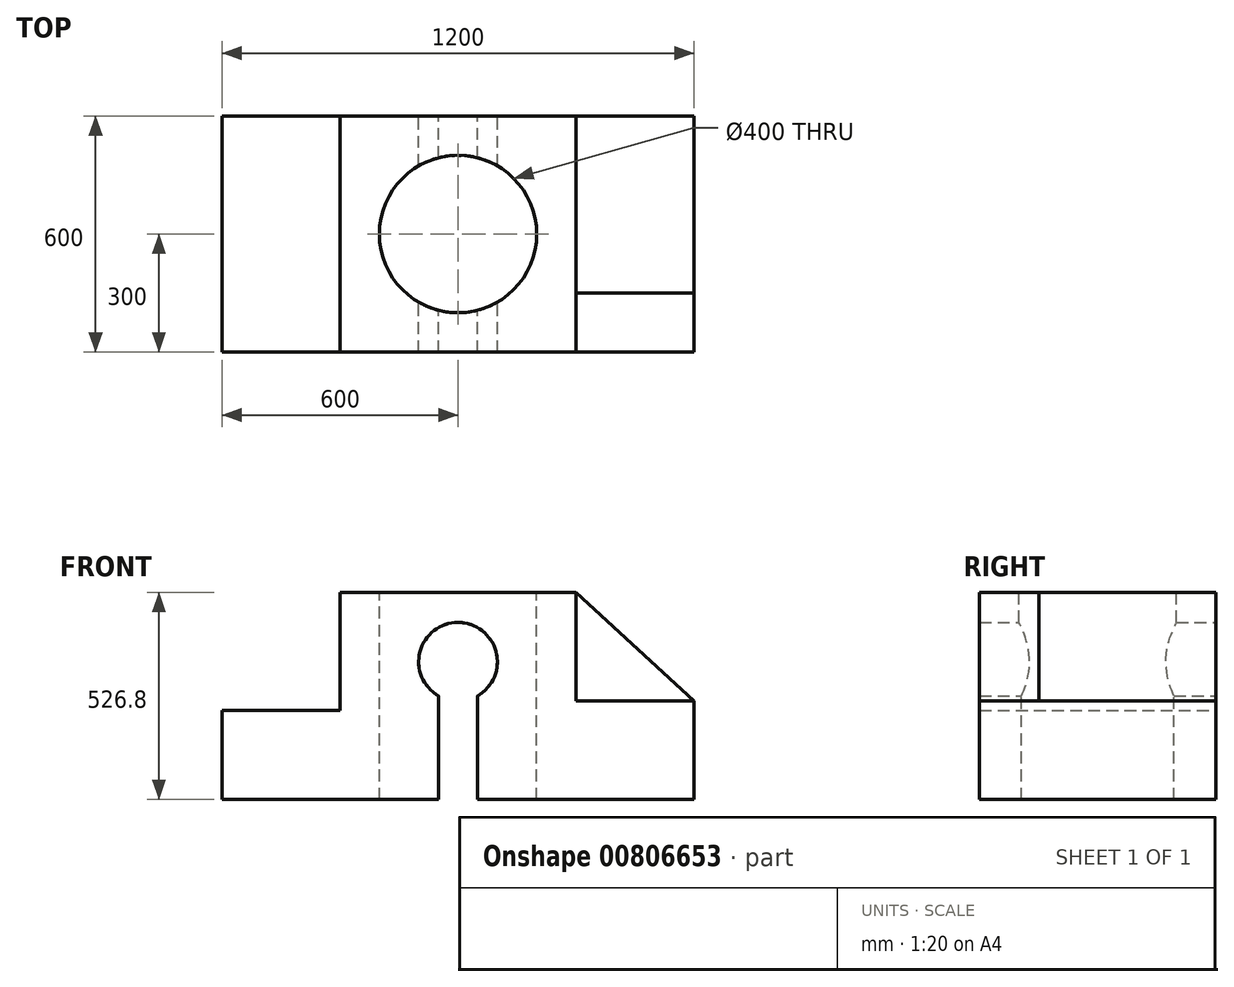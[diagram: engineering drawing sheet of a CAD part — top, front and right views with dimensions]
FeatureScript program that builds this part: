
annotation { "Feature Type Name" : "Feature", "Feature Type Description" : "" }
export const myFeature = defineFeature(function(context is Context, id is Id, definition is map)
    precondition{}
    {
        {
            var Q0;
            Q0=qCreatedBy(makeId("Front.planeOp"),FACE);
            var sketch = newSketch(context, id + "F0", { "sketchPlane" : qUnion([Q0])});
            skLineSegment(sketch, "E0.bottom", {"start": v(300, 263.4) * mm, "end": v(-300, 263.4) * mm});
            skLineSegment(sketch, "E0.top", {"start": v(600, -263.4) * mm, "end": v(50, -263.4) * mm});
            skLineSegment(sketch, "E0.left", {"start": v(600, -13.4) * mm, "end": v(600, -263.4) * mm});
            skLineSegment(sketch, "E0.right", {"start": v(-600, -36.6) * mm, "end": v(-600, -263.4) * mm});
            skPoint(sketch, "E0.middle", {"position": v(0, 0) * mm});
            skLineSegment(sketch, "E1", {"start": v(300, 263.4) * mm, "end": v(300, -13.4) * mm});
            skLineSegment(sketch, "E2", {"start": v(300, -13.4) * mm, "end": v(600, -13.4) * mm});
            skLineSegment(sketch, "E3", {"start": v(-300, 263.4) * mm, "end": v(-300, -36.6) * mm});
            skLineSegment(sketch, "E4", {"start": v(-300, -36.6) * mm, "end": v(-600, -36.6) * mm});
            skLineSegment(sketch, "E5", {"start": v(600, -263.4) * mm, "end": v(600, -13.4) * mm});
            skPoint(sketch, "E6.orphan", {"position": v(-600, 263.4) * mm});
            skPoint(sketch, "E7.orphan", {"position": v(600, 263.4) * mm});
            skArc(sketch, "E8", {"start": v(50, 0) * mm, "mid": v(0, 186.6) * mm, "end": v(-50, 0) * mm});
            skLineSegment(sketch, "E9.left", {"start": v(50, 0) * mm, "end": v(50, -263.4) * mm});
            skLineSegment(sketch, "E9.right", {"start": v(-50, 0) * mm, "end": v(-50, -263.4) * mm});
            skPoint(sketch, "E9.middle", {"position": v(0, -263.4) * mm});
            skPoint(sketch, "E10.orphan", {"position": v(-50, -526.8) * mm});
            skPoint(sketch, "E11.orphan", {"position": v(50, -526.8) * mm});
            skLineSegment(sketch, "E12.trimOffspring", {"start": v(-50, -263.4) * mm, "end": v(-600, -263.4) * mm});
            skSolve(sketch);
        }
        {
            var Q0;
            Q0 = qSketchRegion(id + "F0", true);
            extrude(context, id + "F1", {"entities" : qUnion([Q0]), "depth" : 600 * mm, "offsetDistance" : 25 * mm});
        }
        {
            var Q0;
            Q0=makeQuery(id+"F1.opExtrude","SWEPT_FACE",FACE,{"disambiguationData":[OSD([sQuery(id+"F0.wireOp",EDGE,"E0.bottom")])]});
            var sketch = newSketch(context, id + "F2", { "sketchPlane" : qUnion([Q0])});
            skCircle(sketch, "E13", {"center": v(0, -300) * mm, "radius": 200 * mm});
            skPoint(sketch, "E13.centerSnap0", {"position": v(-300, -300) * mm});
            skSolve(sketch);
        }
        {
            var Q0;
            Q0=makeQuery(id+"F2.imprint","IMPRINT",FACE,{"disambiguationData":[TD([[makeQuery(id+"F2.imprint","IMPRINT",EDGE,{"derivedFrom":sQuery(id+"F2.wireOp",EDGE,"E13")}),1.0]])]});
            extrude(context, id + "F3", {"entities" : qUnion([Q0]), "operationType" : NewBodyOperationType.REMOVE, "endBound" : BoundingType.THROUGH_ALL, "oppositeDirection" : true, "depth" : 25 * mm, "offsetDistance" : 25 * mm});
        }
        {
            var Q0;
            Q0=makeQuery(id+"F1.opExtrude","CAP_FACE",FACE,{"disambiguationData":[OSD([sQuery(id+"F0.wireOp",EDGE,"E0.top"),sQuery(id+"F0.wireOp",EDGE,"E0.right"),sQuery(id+"F0.wireOp",EDGE,"E1"),sQuery(id+"F0.wireOp",EDGE,"E2"),sQuery(id+"F0.wireOp",EDGE,"E3"),sQuery(id+"F0.wireOp",EDGE,"E4"),sQuery(id+"F0.wireOp",EDGE,"E0.bottom"),sQuery(id+"F0.wireOp",EDGE,"E5"),sQuery(id+"F0.wireOp",EDGE,"E8"),sQuery(id+"F0.wireOp",EDGE,"E9.left"),sQuery(id+"F0.wireOp",EDGE,"E9.right"),sQuery(id+"F0.wireOp",EDGE,"E12.trimOffspring")])],"isStart":false});
            var sketch = newSketch(context, id + "F4", { "sketchPlane" : qUnion([Q0])});
            skLineSegment(sketch, "E14", {"start": v(300, 263.4) * mm, "end": v(600, -13.4) * mm});
            skSolve(sketch);
        }
        {
            var Q0;
            Q0 = qSketchRegion(id + "F4", true);
            var Q1;
            Q1=makeQuery(id+"F4.imprint","IMPRINT",FACE,{"disambiguationData":[TD([[makeQuery(id+"F4.imprint","IMPRINT",EDGE,{"derivedFrom":sQuery(id+"F4.wireOp",EDGE,"E14")}),-1.0]])]});
            extrude(context, id + "F5", {"entities" : qUnion([Q0, Q1]), "oppositeDirection" : true, "depth" : 150 * mm, "offsetDistance" : 25 * mm});
        }
    });
